# Revit family: 318_2d1f4eed0aa94340ba20aa5c749ce9
name_source: partatom
category: Pipe Accessories
units: mm (PartAtom-declared; Revit-internal decimal feet)

## family parameters
Always vertical = Yes
Cut with Voids When Loaded = No
Part Type = Valve - Normal
Round Connector Dimension = Use Diameter
Shared = No
Work Plane-Based = No

## types (1)
- FAR-3825 1
    B = 36 mm  [stored 0.11811 ft]
    B1 = 12 mm  [stored 0.0393701 ft]
    B1__ve = -12 mm  [stored -0.0393701 ft]
    B2 = 24 mm  [stored 0.0787402 ft]
    B2__ve = -24 mm  [stored -0.0787402 ft]
    BP = 20 mm
    C1 = 23 mm
    CAT0 = Yes
    CenSd_R_6 = 18 mm
    Description = MULTIFAR 1" chrome modular manifold m-f, 2 ports m24x19
    E1 = 26 mm
    E1__ve = -26 mm
    E2 = 5 mm  [stored 0.0164042 ft]
    E2__ve = -5 mm  [stored -0.0164042 ft]
    E3 = 16 mm
    E3__ve = -16 mm
    L = 98
    L1 = 12 mm  [stored 0.0393701 ft]
    L1__ve = -12 mm  [stored -0.0393701 ft]
    L2 = 3 mm  [stored 0.00984252 ft]
    L3 = 83 mm
    L3__ve = -83 mm
    L4 = 10 mm  [stored 0.0328084 ft]
    L4__ve = -10 mm  [stored -0.0328084 ft]
    L5 = 41 mm
    MP1 = 25 mm
    MP2 = 25 mm
    Manufacturer = FAR
    QmdConnectorList = 301;MP1;302;MP2;303;BP;304;BP
    R = 21 mm  [stored 0.0688976 ft]
    R1 = 13 mm
    R10 = 14 mm  [stored 0.0459318 ft]
    R12 = 14 mm  [stored 0.0459318 ft]
    R3 = 17 mm
    R4 = 10 mm  [stored 0.0328084 ft]
    R6 = 11 mm  [stored 0.0360892 ft]
    R8 = 12 mm  [stored 0.0393701 ft]
    URL = www.far.eu
    magiPartTypeId = 318
    magiProductCode = FAR-3825 1
    magiProductFamilyId = 2d1f4eed0aa94340ba20aa5c749ce9
    magiProductId = 2d1f4eed0aa94340ba20aa5c749ce9

note: [stored X ft] marks values corroborated as IEEE doubles in the binary element streams (Revit-internal decimal feet)

## geometry (parser evidence)
native form markers: Sweep x2
no freeform markers — native parametric forms only
